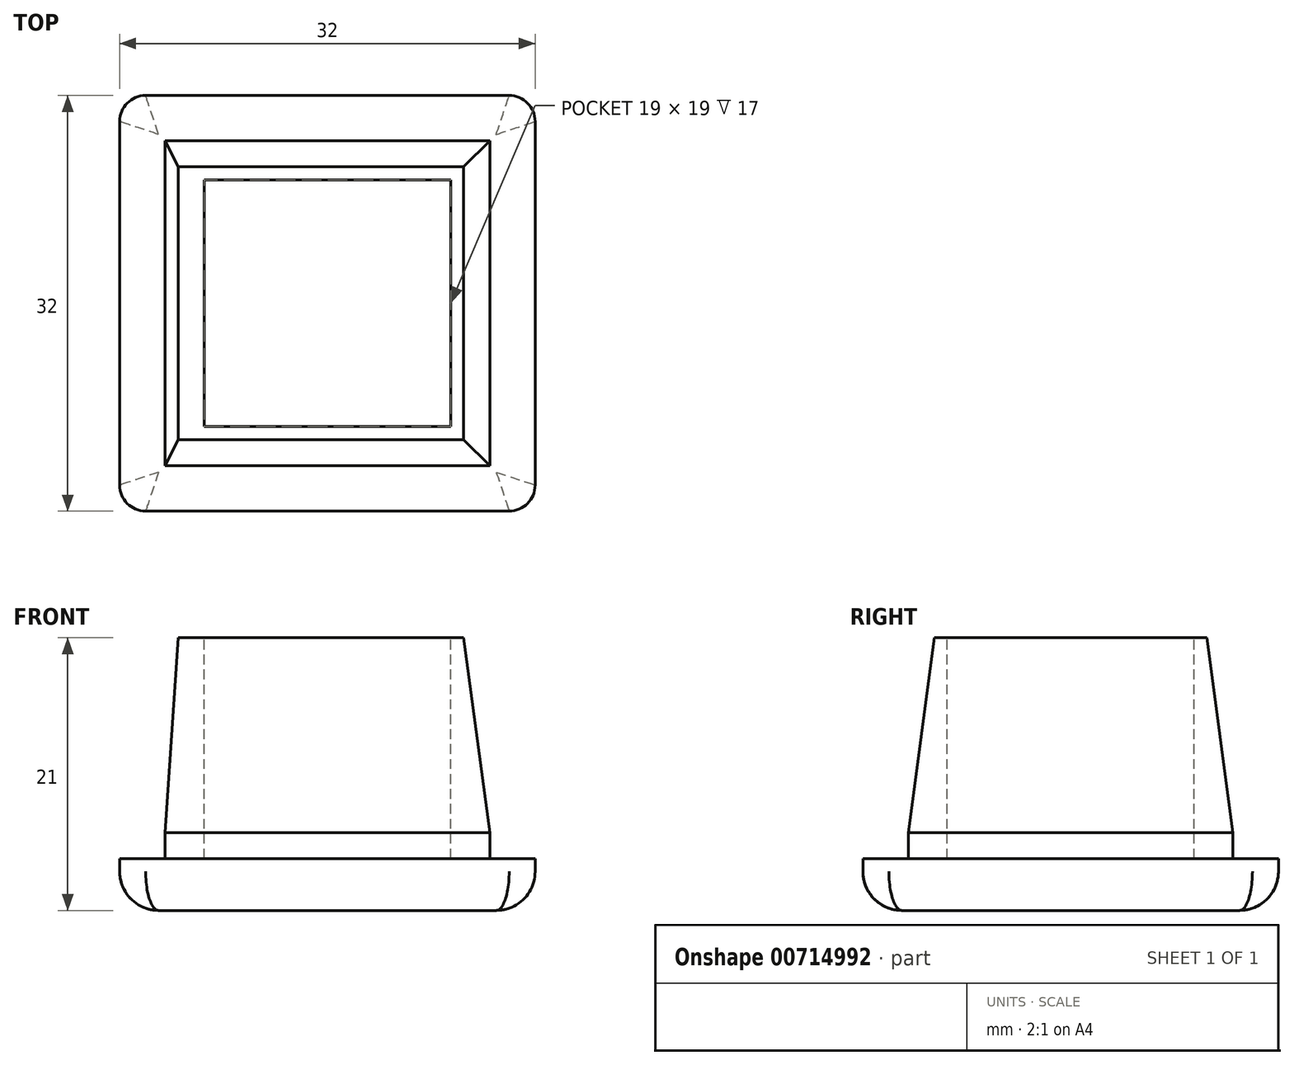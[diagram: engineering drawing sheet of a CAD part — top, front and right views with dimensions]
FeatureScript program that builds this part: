
annotation { "Feature Type Name" : "Feature", "Feature Type Description" : "" }
export const myFeature = defineFeature(function(context is Context, id is Id, definition is map)
    precondition{}
    {
        {
            var Q0;
            Q0=qCreatedBy(makeId("Top.planeOp"),FACE);
            var sketch = newSketch(context, id + "F0", { "sketchPlane" : qUnion([Q0])});
            skLineSegment(sketch, "E0.bottom", {"start": v(-5.38, 4.8) * mm, "end": v(26.62, 4.8) * mm});
            skLineSegment(sketch, "E0.top", {"start": v(-5.38, -27.2) * mm, "end": v(26.62, -27.2) * mm});
            skLineSegment(sketch, "E0.left", {"start": v(-5.38, 4.8) * mm, "end": v(-5.38, -27.2) * mm});
            skLineSegment(sketch, "E0.right", {"start": v(26.62, 4.8) * mm, "end": v(26.62, -27.2) * mm});
            skSolve(sketch);
        }
        {
            var Q0;
            Q0=makeQuery(id+"F0.imprint","IMPRINT",FACE,{"disambiguationData":[TD([[makeQuery(id+"F0.imprint","IMPRINT",EDGE,{"derivedFrom":sQuery(id+"F0.wireOp",EDGE,"E0.bottom")}),-1.0]])]});
            extrude(context, id + "F1", {"entities" : qUnion([Q0]), "depth" : 4 * mm, "offsetDistance" : 25 * mm});
        }
        {
            var Q0;
            Q0=makeQuery(id+"F1.opExtrude","CAP_FACE",FACE,{"disambiguationData":[OSD([sQuery(id+"F0.wireOp",EDGE,"E0.bottom"),sQuery(id+"F0.wireOp",EDGE,"E0.top"),sQuery(id+"F0.wireOp",EDGE,"E0.left"),sQuery(id+"F0.wireOp",EDGE,"E0.right")])],"isStart":false});
            var sketch = newSketch(context, id + "F2", { "sketchPlane" : qUnion([Q0])});
            skLineSegment(sketch, "E1.bottom", {"start": v(-5.38, 4.8) * mm, "end": v(-1.88, 4.8) * mm});
            skLineSegment(sketch, "E1.top", {"start": v(-5.38, 1.3) * mm, "end": v(-1.88, 1.3) * mm});
            skLineSegment(sketch, "E1.left", {"start": v(-5.38, 4.8) * mm, "end": v(-5.38, 1.3) * mm});
            skLineSegment(sketch, "E1.right", {"start": v(-1.88, 4.8) * mm, "end": v(-1.88, 1.3) * mm});
            skLineSegment(sketch, "E2.bottom", {"start": v(26.62, -27.2) * mm, "end": v(23.12, -27.2) * mm});
            skLineSegment(sketch, "E2.top", {"start": v(26.62, -23.7) * mm, "end": v(23.12, -23.7) * mm});
            skLineSegment(sketch, "E2.left", {"start": v(26.62, -27.2) * mm, "end": v(26.62, -23.7) * mm});
            skLineSegment(sketch, "E2.right", {"start": v(23.12, -27.2) * mm, "end": v(23.12, -23.7) * mm});
            skLineSegment(sketch, "E3.bottom", {"start": v(23.12, -23.7) * mm, "end": v(-1.88, -23.7) * mm});
            skLineSegment(sketch, "E3.top", {"start": v(23.12, 1.3) * mm, "end": v(-1.88, 1.3) * mm});
            skLineSegment(sketch, "E3.left", {"start": v(23.12, -23.7) * mm, "end": v(23.12, 1.3) * mm});
            skLineSegment(sketch, "E3.right", {"start": v(-1.88, -23.7) * mm, "end": v(-1.88, 1.3) * mm});
            skSolve(sketch);
        }
        {
            var Q0;
            Q0=makeQuery(id+"F2.imprint","IMPRINT",FACE,{"disambiguationData":[TD([[makeQuery(id+"F2.imprint","IMPRINT",EDGE,{"derivedFrom":sQuery(id+"F2.wireOp",EDGE,"E3.bottom")}),-1.0]])]});
            extrude(context, id + "F3", {"entities" : qUnion([Q0]), "operationType" : NewBodyOperationType.ADD, "depth" : 17 * mm, "offsetDistance" : 25 * mm});
        }
        {
            var Q0;
            Q0=makeQuery(id+"F3.opExtrude","CAP_FACE",FACE,{"disambiguationData":[OSD([sQuery(id+"F2.wireOp",EDGE,"E3.bottom"),sQuery(id+"F2.wireOp",EDGE,"E3.top"),sQuery(id+"F2.wireOp",EDGE,"E3.left"),sQuery(id+"F2.wireOp",EDGE,"E3.right")])],"isStart":false});
            var sketch = newSketch(context, id + "F4", { "sketchPlane" : qUnion([Q0])});
            skLineSegment(sketch, "E4.bottom", {"start": v(-1.88, 1.3) * mm, "end": v(1.12, 1.3) * mm});
            skLineSegment(sketch, "E4.top", {"start": v(-1.88, -1.7) * mm, "end": v(1.12, -1.7) * mm});
            skLineSegment(sketch, "E4.left", {"start": v(-1.88, 1.3) * mm, "end": v(-1.88, -1.7) * mm});
            skLineSegment(sketch, "E4.right", {"start": v(1.12, 1.3) * mm, "end": v(1.12, -1.7) * mm});
            skLineSegment(sketch, "E5.bottom", {"start": v(23.12, -23.7) * mm, "end": v(20.12, -23.7) * mm});
            skLineSegment(sketch, "E5.top", {"start": v(23.12, -20.7) * mm, "end": v(20.12, -20.7) * mm});
            skLineSegment(sketch, "E5.left", {"start": v(23.12, -23.7) * mm, "end": v(23.12, -20.7) * mm});
            skLineSegment(sketch, "E5.right", {"start": v(20.12, -23.7) * mm, "end": v(20.12, -20.7) * mm});
            skLineSegment(sketch, "E6.bottom", {"start": v(1.12, -1.7) * mm, "end": v(20.12, -1.7) * mm});
            skLineSegment(sketch, "E6.top", {"start": v(1.12, -20.7) * mm, "end": v(20.12, -20.7) * mm});
            skLineSegment(sketch, "E6.left", {"start": v(1.12, -1.7) * mm, "end": v(1.12, -20.7) * mm});
            skLineSegment(sketch, "E6.right", {"start": v(20.12, -1.7) * mm, "end": v(20.12, -20.7) * mm});
            skSolve(sketch);
        }
        {
            var Q0;
            Q0=makeQuery(id+"F4.imprint","IMPRINT",FACE,{"disambiguationData":[TD([[makeQuery(id+"F4.imprint","IMPRINT",EDGE,{"derivedFrom":sQuery(id+"F4.wireOp",EDGE,"E6.bottom")}),-1.0]])]});
            extrude(context, id + "F5", {"entities" : qUnion([Q0]), "operationType" : NewBodyOperationType.REMOVE, "oppositeDirection" : true, "depth" : 17 * mm, "offsetDistance" : 25 * mm});
        }
        {
            var Q0;
            Q0=makeQuery(id+"F3.opExtrude","CAP_EDGE",EDGE,{"disambiguationData":[OSD([sQuery(id+"F2.wireOp",EDGE,"E3.right")])],"isStart":false});
            chamfer(context, id + "F6", {"entities" : qUnion([Q0]), "chamferType" : ChamferType.TWO_OFFSETS, "width1" : 15 * mm, "oppositeDirection" : false, "width2" : 1 * mm, "tangentPropagation" : true});
        }
        {
            var Q0;
            Q0=makeQuery(id+"F3.opExtrude","CAP_EDGE",EDGE,{"disambiguationData":[OSD([sQuery(id+"F2.wireOp",EDGE,"E3.bottom")])],"isStart":false});
            chamfer(context, id + "F7", {"entities" : qUnion([Q0]), "chamferType" : ChamferType.TWO_OFFSETS, "width1" : 15 * mm, "oppositeDirection" : false, "width2" : 2 * mm, "tangentPropagation" : true});
        }
        {
            var Q0;
            Q0=makeQuery(id+"F3.opExtrude","CAP_EDGE",EDGE,{"disambiguationData":[OSD([sQuery(id+"F2.wireOp",EDGE,"E3.top")])],"isStart":false});
            chamfer(context, id + "F8", {"entities" : qUnion([Q0]), "chamferType" : ChamferType.TWO_OFFSETS, "width1" : 2 * mm, "oppositeDirection" : false, "width2" : 15 * mm, "tangentPropagation" : true});
        }
        {
            var Q0;
            Q0=makeQuery(id+"F3.opExtrude","CAP_EDGE",EDGE,{"disambiguationData":[OSD([sQuery(id+"F2.wireOp",EDGE,"E3.left")])],"isStart":false});
            chamfer(context, id + "F9", {"entities" : qUnion([Q0]), "chamferType" : ChamferType.TWO_OFFSETS, "width1" : 2 * mm, "oppositeDirection" : false, "width2" : 15 * mm, "tangentPropagation" : true});
        }
        {
            var Q0;
            Q0=makeQuery(id+"F1.opExtrude","SWEPT_EDGE",EDGE,{"disambiguationData":[OSD([sQuery(id+"F0.wireOp",EDGE,"E0.top"),sQuery(id+"F0.wireOp",EDGE,"E0.left")])]});
            fillet(context, id + "F10", {"entities" : qUnion([Q0]), "radius" : 2 * mm, "tangentPropagation" : true, "allowEdgeOverflow" : false});
        }
        {
            var Q0;
            Q0=makeQuery(id+"F1.opExtrude","SWEPT_EDGE",EDGE,{"disambiguationData":[OSD([sQuery(id+"F0.wireOp",EDGE,"E0.top"),sQuery(id+"F0.wireOp",EDGE,"E0.right")])]});
            var Q1;
            Q1=makeQuery(id+"F1.opExtrude","SWEPT_EDGE",EDGE,{"disambiguationData":[OSD([sQuery(id+"F0.wireOp",EDGE,"E0.bottom"),sQuery(id+"F0.wireOp",EDGE,"E0.right")])]});
            var Q2;
            Q2=makeQuery(id+"F1.opExtrude","SWEPT_EDGE",EDGE,{"disambiguationData":[OSD([sQuery(id+"F0.wireOp",EDGE,"E0.bottom"),sQuery(id+"F0.wireOp",EDGE,"E0.left")])]});
            fillet(context, id + "F11", {"entities" : qUnion([Q0, Q1, Q2]), "radius" : 2 * mm, "tangentPropagation" : true, "allowEdgeOverflow" : false});
        }
        {
            var Q0;
            Q0=makeQuery(id+"F1.opExtrude","CAP_EDGE",EDGE,{"disambiguationData":[OSD([sQuery(id+"F0.wireOp",EDGE,"E0.left")])],"isStart":true});
            fillet(context, id + "F12", {"entities" : qUnion([Q0]), "radius" : 3 * mm, "tangentPropagation" : true, "allowEdgeOverflow" : false});
        }
    });
